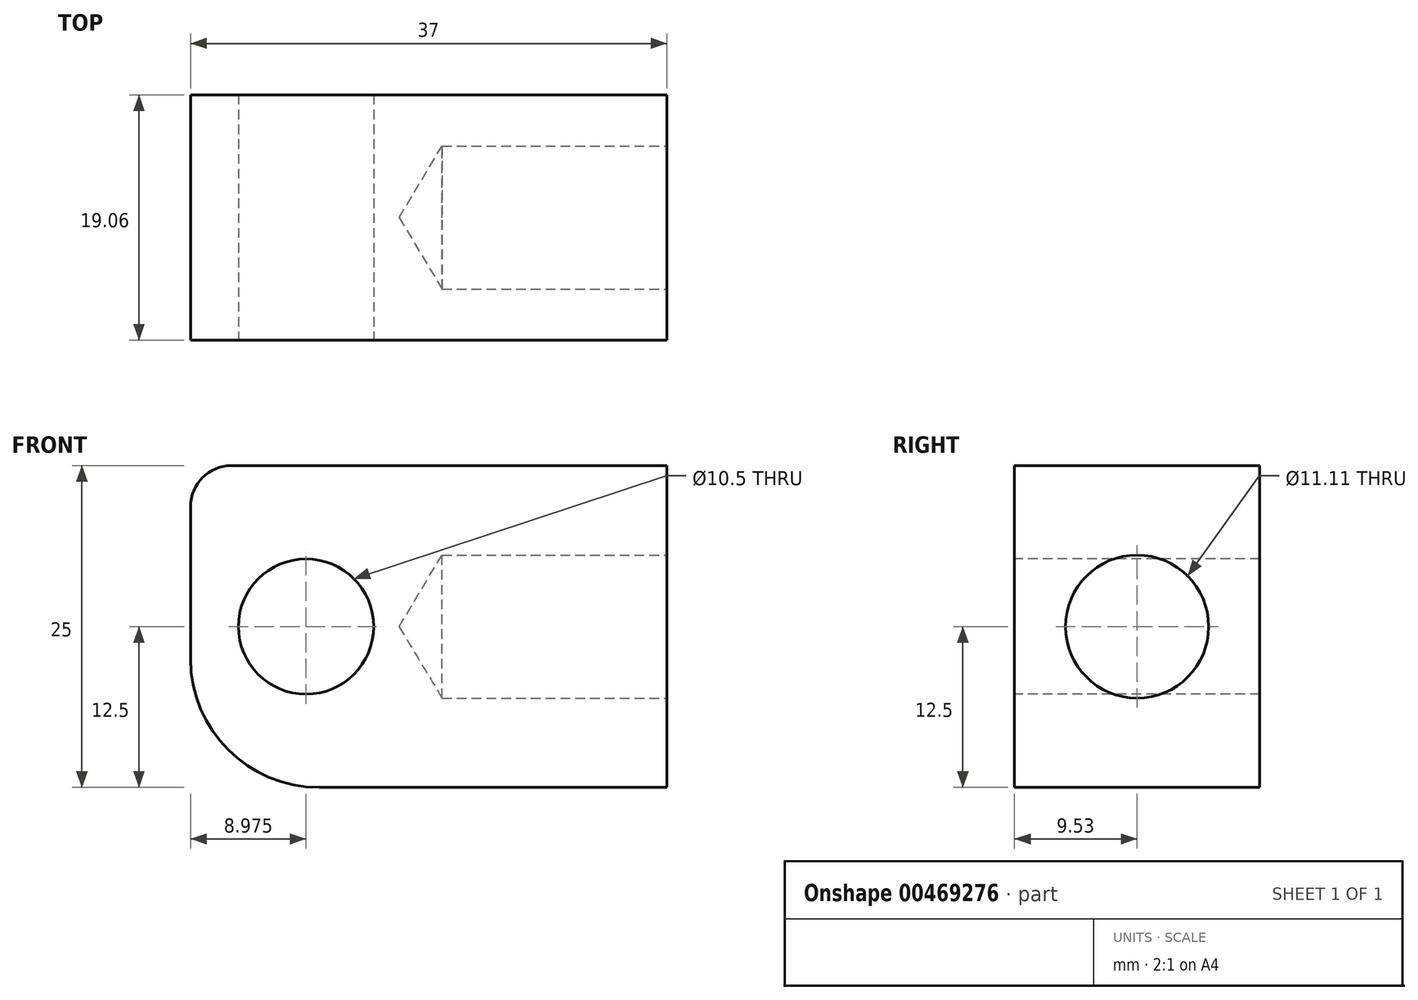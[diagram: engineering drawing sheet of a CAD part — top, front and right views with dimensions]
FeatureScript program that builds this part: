
annotation { "Feature Type Name" : "Feature", "Feature Type Description" : "" }
export const myFeature = defineFeature(function(context is Context, id is Id, definition is map)
    precondition{}
    {
        {
            var Q0;
            Q0=qCreatedBy(makeId("Front.planeOp"),FACE);
            var sketch = newSketch(context, id + "F0", { "sketchPlane" : qUnion([Q0])});
            skLineSegment(sketch, "E0.rect.bottom", {"start": v(-18.5, -12.5) * mm, "end": v(18.5, -12.5) * mm});
            skLineSegment(sketch, "E0.rect.top", {"start": v(-18.5, 12.5) * mm, "end": v(18.5, 12.5) * mm});
            skLineSegment(sketch, "E0.rect.left", {"start": v(-18.5, -12.5) * mm, "end": v(-18.5, 12.5) * mm});
            skLineSegment(sketch, "E0.rect.right", {"start": v(18.5, -12.5) * mm, "end": v(18.5, 12.5) * mm});
            skSolve(sketch);
        }
        {
            var Q0;
            Q0=qCreatedBy(makeId("Front.planeOp"),FACE);
            var sketch = newSketch(context, id + "F1", { "sketchPlane" : qUnion([Q0])});
            skCircle(sketch, "E1", {"center": v(-9.53, 0) * mm, "radius": 5.25 * mm});
            skSolve(sketch);
        }
        {
            var Q0;
            Q0=makeQuery(id+"F0.imprint","IMPRINT",FACE,{"disambiguationData":[TD([[makeQuery(id+"F0.imprint","IMPRINT",EDGE,{"derivedFrom":sQuery(id+"F0.wireOp",EDGE,"E0.rect.bottom")}),1.0]])]});
            extrude(context, id + "F2", {"entities" : qUnion([Q0]), "endBound" : BoundingType.SYMMETRIC, "depth" : 19.05 * mm});
        }
        {
            var Q0;
            Q0=qSketchRegion(id+"F1",true);
            extrude(context, id + "F3", {"entities" : qUnion([Q0]), "operationType" : NewBodyOperationType.REMOVE, "endBound" : BoundingType.SYMMETRIC, "oppositeDirection" : true, "depth" : 25 * mm});
        }
        {
            var Q0;
            Q0=makeQuery(id+"F2.opExtrude","SWEPT_EDGE",EDGE,{"disambiguationData":[OSD([sQuery(id+"F0.wireOp",EDGE,"E0.rect.bottom"),sQuery(id+"F0.wireOp",EDGE,"E0.rect.left")])]});
            fillet(context, id + "F4", {"entities" : qUnion([Q0]), "radius" : 10 * mm, "tangentPropagation" : true, "allowEdgeOverflow" : false});
        }
        {
            var Q0;
            Q0=makeQuery(id+"F2.opExtrude","SWEPT_FACE",FACE,{"disambiguationData":[OSD([sQuery(id+"F0.wireOp",EDGE,"E0.rect.right")])]});
            var sketch = newSketch(context, id + "F5", { "sketchPlane" : qUnion([Q0])});
            skCircle(sketch, "E2", {"center": v(0, 0) * mm, "radius": 0.19 * mm});
            skSolve(sketch);
        }
        {
            var Q0;
            Q0=sQuery(id+"F5.wireOp",VERTEX,"E2.center");
            var Q1;
            Q1=makeQuery(id+"F2.opExtrude","SWEPT_BODY",BODY,{"disambiguationData":[OSD([sQuery(id+"F0.wireOp",EDGE,"E0.rect.bottom"),sQuery(id+"F0.wireOp",EDGE,"E0.rect.top"),sQuery(id+"F0.wireOp",EDGE,"E0.rect.left"),sQuery(id+"F0.wireOp",EDGE,"E0.rect.right")])]});
            hole(context, id + "F6", {"style" : HoleStyle.SIMPLE, "holeDiameter" : 11.1 * mm, "endStyle" : HoleEndStyle.BLIND, "holeDepth" : 17.46 * mm, "locations" : qUnion([Q0]), "scope" : qUnion([Q1])});
        }
        {
            var Q0;
            Q0=makeQuery(id+"F2.opExtrude","SWEPT_EDGE",EDGE,{"disambiguationData":[OSD([sQuery(id+"F0.wireOp",EDGE,"E0.rect.top"),sQuery(id+"F0.wireOp",EDGE,"E0.rect.left")])]});
            fillet(context, id + "F7", {"entities" : qUnion([Q0]), "radius" : 3.17 * mm, "tangentPropagation" : true, "allowEdgeOverflow" : false});
        }
    });
